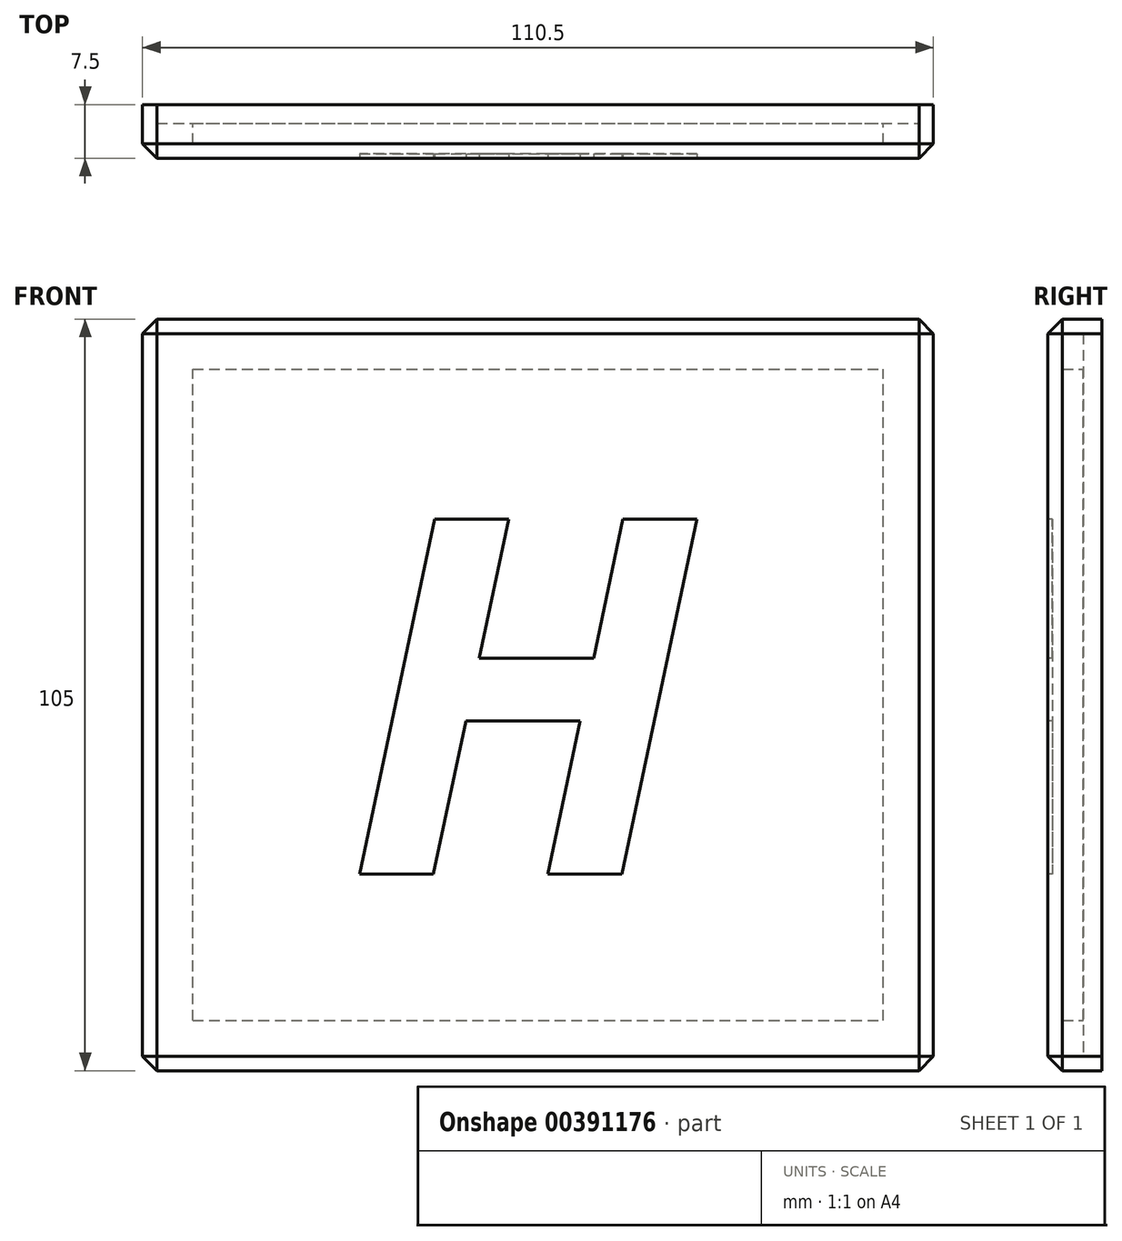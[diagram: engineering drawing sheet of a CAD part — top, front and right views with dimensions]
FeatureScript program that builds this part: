
annotation { "Feature Type Name" : "Feature", "Feature Type Description" : "" }
export const myFeature = defineFeature(function(context is Context, id is Id, definition is map)
    precondition{}
    {
        {
            var Q0;
            Q0=qCreatedBy(makeId("Front.planeOp"),FACE);
            var sketch = newSketch(context, id + "F0", { "sketchPlane" : qUnion([Q0])});
            skLineSegment(sketch, "E0.bottom", {"start": v(-53.25, 50.5) * mm, "end": v(53.25, 50.5) * mm});
            skLineSegment(sketch, "E0.top", {"start": v(-53.25, -50.5) * mm, "end": v(53.25, -50.5) * mm});
            skLineSegment(sketch, "E0.left", {"start": v(-53.25, 50.5) * mm, "end": v(-53.25, -50.5) * mm});
            skLineSegment(sketch, "E0.right", {"start": v(53.25, 50.5) * mm, "end": v(53.25, -50.5) * mm});
            skSolve(sketch);
        }
        {
            var Q0;
            Q0=qCreatedBy(makeId("Front.planeOp"),FACE);
            var sketch = newSketch(context, id + "F1", { "sketchPlane" : qUnion([Q0])});
            skLineSegment(sketch, "E1.bottom", {"start": v(-55.25, 52.5) * mm, "end": v(55.25, 52.5) * mm});
            skLineSegment(sketch, "E1.top", {"start": v(-55.25, -52.5) * mm, "end": v(55.25, -52.5) * mm});
            skLineSegment(sketch, "E1.left", {"start": v(-55.25, 52.5) * mm, "end": v(-55.25, -52.5) * mm});
            skLineSegment(sketch, "E1.right", {"start": v(55.25, 52.5) * mm, "end": v(55.25, -52.5) * mm});
            skSolve(sketch);
        }
        {
            var Q0;
            Q0 = qSketchRegion(id + "F1", true);
            extrude(context, id + "F2", {"entities" : qUnion([Q0]), "depth" : 7.5 * mm});
        }
        {
            var Q0;
            Q0 = qSketchRegion(id + "F0", true);
            extrude(context, id + "F3", {"entities" : qUnion([Q0]), "operationType" : NewBodyOperationType.REMOVE, "depth" : 2.6 * mm});
        }
        {
            var Q0;
            Q0=qCreatedBy(makeId("Front.planeOp"),FACE);
            var sketch = newSketch(context, id + "F4", { "sketchPlane" : qUnion([Q0])});
            skLineSegment(sketch, "E2.bottom", {"start": v(48.25, 45.5) * mm, "end": v(-48.25, 45.5) * mm});
            skLineSegment(sketch, "E2.top", {"start": v(48.25, -45.5) * mm, "end": v(-48.25, -45.5) * mm});
            skLineSegment(sketch, "E2.left", {"start": v(48.25, 45.5) * mm, "end": v(48.25, -45.5) * mm});
            skLineSegment(sketch, "E2.right", {"start": v(-48.25, 45.5) * mm, "end": v(-48.25, -45.5) * mm});
            skSolve(sketch);
        }
        {
            var Q0;
            Q0 = qSketchRegion(id + "F4", true);
            extrude(context, id + "F5", {"entities" : qUnion([Q0]), "operationType" : NewBodyOperationType.REMOVE, "depth" : 5.5 * mm});
        }
        {
            var Q0;
            Q0=makeQuery(id+"F2.opExtrude","CAP_FACE",FACE,{"disambiguationData":[OSD([sQuery(id+"F1.wireOp",EDGE,"E1.bottom"),sQuery(id+"F1.wireOp",EDGE,"E1.top"),sQuery(id+"F1.wireOp",EDGE,"E1.left"),sQuery(id+"F1.wireOp",EDGE,"E1.right")])],"isStart":false});
            var sketch = newSketch(context, id + "F6", { "sketchPlane" : qUnion([Q0])});
            skText(sketch, "E3", { "text": "H", "fontName": "OpenSans-BoldItalic.ttf"});
            const initialGuessF6  = {"E3": [-0.02674, -0.025, 1, 0, 0.05]};
            skSetInitialGuess(sketch, initialGuessF6);
            skSolve(sketch);
        }
        {
            var Q0;
            Q0 = qSketchRegion(id + "F6", true);
            extrude(context, id + "F7", {"entities" : qUnion([Q0]), "operationType" : NewBodyOperationType.REMOVE, "oppositeDirection" : true, "depth" : .6 * mm});
        }
        {
            var Q0;
            Q0=makeQuery(id+"F2.opExtrude","SWEPT_EDGE",EDGE,{"disambiguationData":[OSD([sQuery(id+"F1.wireOp",EDGE,"E1.bottom"),sQuery(id+"F1.wireOp",EDGE,"E1.right")])]});
            var Q1;
            Q1=makeQuery(id+"F2.opExtrude","SWEPT_EDGE",EDGE,{"disambiguationData":[OSD([sQuery(id+"F1.wireOp",EDGE,"E1.bottom"),sQuery(id+"F1.wireOp",EDGE,"E1.left")])]});
            var Q2;
            Q2=makeQuery(id+"F2.opExtrude","SWEPT_EDGE",EDGE,{"disambiguationData":[OSD([sQuery(id+"F1.wireOp",EDGE,"E1.top"),sQuery(id+"F1.wireOp",EDGE,"E1.right")])]});
            var Q3;
            Q3=makeQuery(id+"F2.opExtrude","SWEPT_EDGE",EDGE,{"disambiguationData":[OSD([sQuery(id+"F1.wireOp",EDGE,"E1.top"),sQuery(id+"F1.wireOp",EDGE,"E1.left")])]});
            var Q4;
            Q4=makeQuery(id+"F2.opExtrude","CAP_EDGE",EDGE,{"disambiguationData":[OSD([sQuery(id+"F1.wireOp",EDGE,"E1.top")])],"isStart":false});
            var Q5;
            Q5=makeQuery(id+"F2.opExtrude","CAP_EDGE",EDGE,{"disambiguationData":[OSD([sQuery(id+"F1.wireOp",EDGE,"E1.left")])],"isStart":false});
            var Q6;
            Q6=makeQuery(id+"F2.opExtrude","CAP_EDGE",EDGE,{"disambiguationData":[OSD([sQuery(id+"F1.wireOp",EDGE,"E1.bottom")])],"isStart":false});
            var Q7;
            Q7=makeQuery(id+"F2.opExtrude","CAP_EDGE",EDGE,{"disambiguationData":[OSD([sQuery(id+"F1.wireOp",EDGE,"E1.right")])],"isStart":false});
            chamfer(context, id + "F8", {"entities" : qUnion([Q0, Q1, Q2, Q3, Q4, Q5, Q6, Q7]), "width" : 2 * mm, "tangentPropagation" : true});
        }
    });
